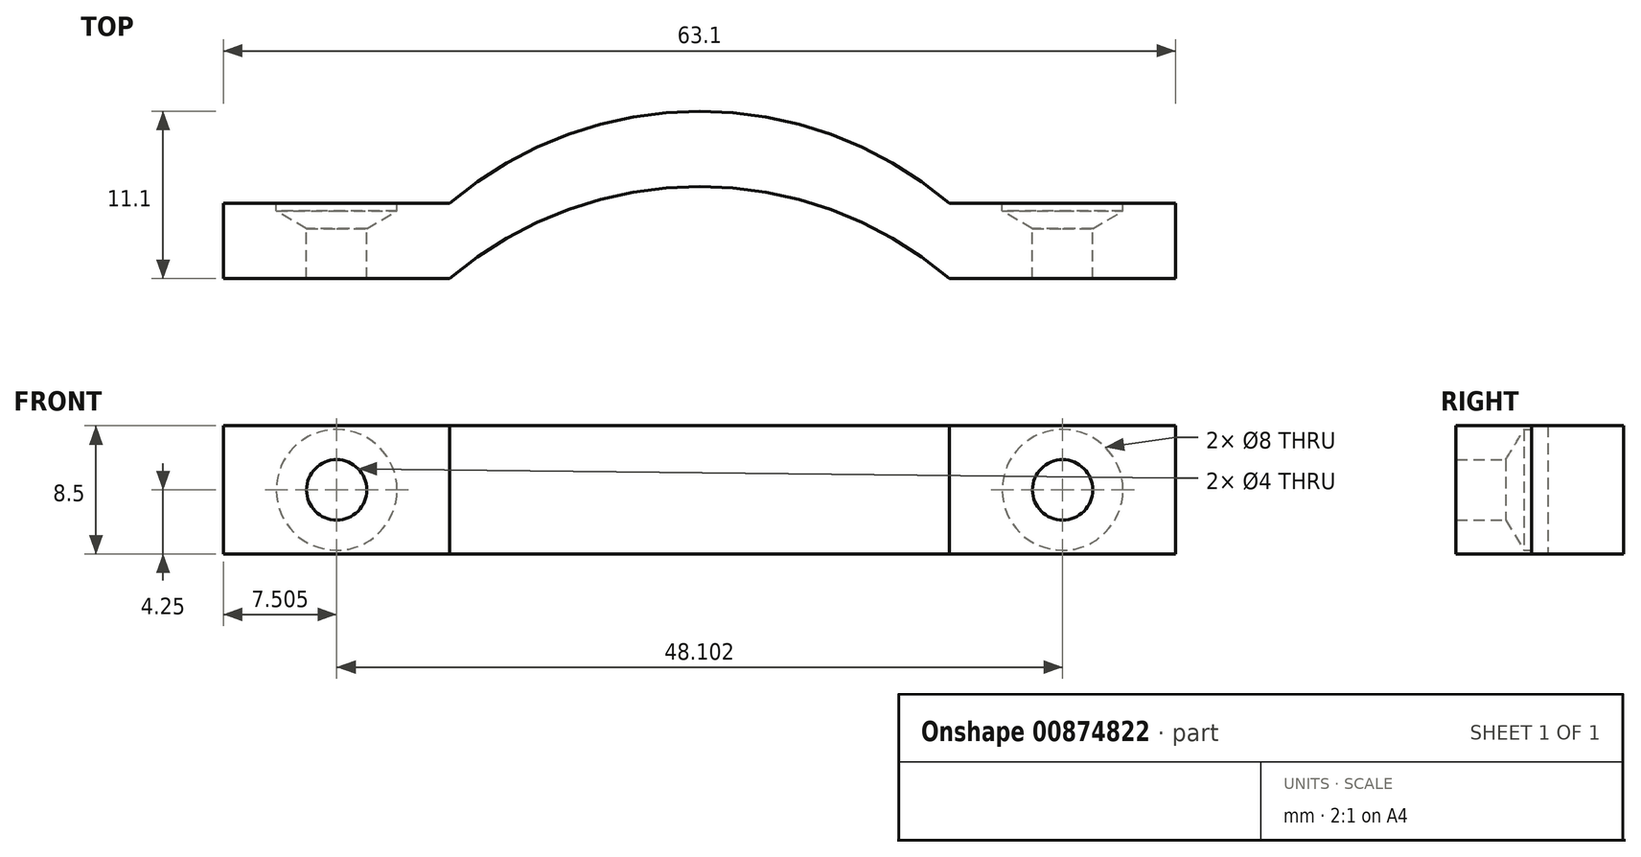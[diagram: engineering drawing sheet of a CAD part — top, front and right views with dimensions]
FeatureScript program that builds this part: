
annotation { "Feature Type Name" : "Feature", "Feature Type Description" : "" }
export const myFeature = defineFeature(function(context is Context, id is Id, definition is map)
    precondition{}
    {
        {
            var Q0;
            Q0=qCreatedBy(makeId("Top.planeOp"),FACE);
            var sketch = newSketch(context, id + "F0", { "sketchPlane" : qUnion([Q0])});
            skArc(sketch, "E0", {"start": v(24.25, 11.33) * mm, "mid": v(7.7, 17.43) * mm, "end": v(-8.85, 11.33) * mm});
            skLineSegment(sketch, "E1", {"start": v(-8.85, 11.33) * mm, "end": v(-23.85, 11.33) * mm});
            skLineSegment(sketch, "E2", {"start": v(24.25, 11.33) * mm, "end": v(39.25, 11.33) * mm});
            skLineSegment(sketch, "E3", {"start": v(-23.85, 11.33) * mm, "end": v(-23.85, 16.33) * mm});
            skLineSegment(sketch, "E4", {"start": v(39.25, 11.33) * mm, "end": v(39.25, 16.33) * mm});
            skLineSegment(sketch, "E5", {"start": v(-23.85, 16.33) * mm, "end": v(-8.85, 16.33) * mm});
            skLineSegment(sketch, "E6", {"start": v(39.25, 16.33) * mm, "end": v(24.25, 16.33) * mm});
            skArc(sketch, "E7", {"start": v(24.25, 16.33) * mm, "mid": v(7.7, 22.43) * mm, "end": v(-8.85, 16.33) * mm});
            skSolve(sketch);
        }
        {
            var Q0;
            Q0=makeQuery(id+"F0.imprint","IMPRINT",FACE,{"disambiguationData":[TD([[makeQuery(id+"F0.imprint","IMPRINT",EDGE,{"derivedFrom":sQuery(id+"F0.wireOp",EDGE,"E0")}),-1.0]])]});
            extrude(context, id + "F1", {"entities" : qUnion([Q0]), "depth" : 8.5 * mm, "offsetDistance" : 25 * mm});
        }
        {
            var Q0;
            Q0=makeQuery(id+"F1.opExtrude","SWEPT_FACE",FACE,{"disambiguationData":[OSD([sQuery(id+"F0.wireOp",EDGE,"E5")])]});
            var sketch = newSketch(context, id + "F2", { "sketchPlane" : qUnion([Q0])});
            skPoint(sketch, "E8", {"position": v(-31.76, 4.25) * mm});
            skCircle(sketch, "E9", {"center": v(-31.76, 4.25) * mm, "radius": 2.5 * mm});
            skCircle(sketch, "E10", {"center": v(-31.76, 4.25) * mm, "radius": 3 * mm});
            skLineSegment(sketch, "E11.bottom", {"start": v(23.85, 0) * mm, "end": v(8.85, 0) * mm});
            skLineSegment(sketch, "E11.top", {"start": v(23.85, 8.5) * mm, "end": v(8.85, 8.5) * mm});
            skLineSegment(sketch, "E11.left", {"start": v(23.85, 0) * mm, "end": v(23.85, 8.5) * mm});
            skLineSegment(sketch, "E11.right", {"start": v(8.85, 0) * mm, "end": v(8.85, 8.5) * mm});
            skPoint(sketch, "E12", {"position": v(16.35, 4.25) * mm});
            skPoint(sketch, "E12.positionSnap0", {"position": v(23.85, 4.25) * mm});
            skPoint(sketch, "E12.positionSnap1", {"position": v(16.35, 8.5) * mm});
            skCircle(sketch, "E13", {"center": v(16.35, 4.25) * mm, "radius": 3 * mm});
            skCircle(sketch, "E14", {"center": v(16.35, 4.25) * mm, "radius": 2.5 * mm});
            skSolve(sketch);
        }
        {
            var Q0;
            Q0=sQuery(id+"F2.wireOp",VERTEX,"E8");
            var Q1;
            Q1=sQuery(id+"F2.wireOp",VERTEX,"E12");
            var Q2;
            Q2=makeQuery(id+"F1.opExtrude","SWEPT_BODY",BODY,{"disambiguationData":[OSD([sQuery(id+"F0.wireOp",EDGE,"E0"),sQuery(id+"F0.wireOp",EDGE,"E1"),sQuery(id+"F0.wireOp",EDGE,"E2"),sQuery(id+"F0.wireOp",EDGE,"E3"),sQuery(id+"F0.wireOp",EDGE,"E4"),sQuery(id+"F0.wireOp",EDGE,"E5"),sQuery(id+"F0.wireOp",EDGE,"E6"),sQuery(id+"F0.wireOp",EDGE,"E7")])]});
            hole(context, id + "F3", {"style" : HoleStyle.SIMPLE, "endStyle" : HoleEndStyle.BLIND, "holeDiameter" : 8 * mm, "majorDiameter" : 5 * mm, "holeDepth" : .5 * mm, "isTappedThrough" : true, "tappedDepth" : 12 * mm, "tapClearance" : 3, "locations" : qUnion([Q0, Q1]), "scope" : qUnion([Q2])});
        }
        {
            var Q0;
            Q0=sQuery(id+"F2.wireOp",VERTEX,"E8");
            var Q1;
            Q1=sQuery(id+"F2.wireOp",VERTEX,"E12");
            var Q2;
            Q2=makeQuery(id+"F1.opExtrude","SWEPT_BODY",BODY,{"disambiguationData":[OSD([sQuery(id+"F0.wireOp",EDGE,"E0"),sQuery(id+"F0.wireOp",EDGE,"E1"),sQuery(id+"F0.wireOp",EDGE,"E2"),sQuery(id+"F0.wireOp",EDGE,"E3"),sQuery(id+"F0.wireOp",EDGE,"E4"),sQuery(id+"F0.wireOp",EDGE,"E5"),sQuery(id+"F0.wireOp",EDGE,"E6"),sQuery(id+"F0.wireOp",EDGE,"E7")])]});
            hole(context, id + "F4", {"style" : HoleStyle.SIMPLE, "endStyle" : HoleEndStyle.BLIND, "holeDiameter" : 4 * mm, "majorDiameter" : 5 * mm, "holeDepth" : 12 * mm, "isTappedThrough" : true, "tappedDepth" : 12 * mm, "tapClearance" : 3, "locations" : qUnion([Q0, Q1]), "scope" : qUnion([Q2])});
        }
    });
